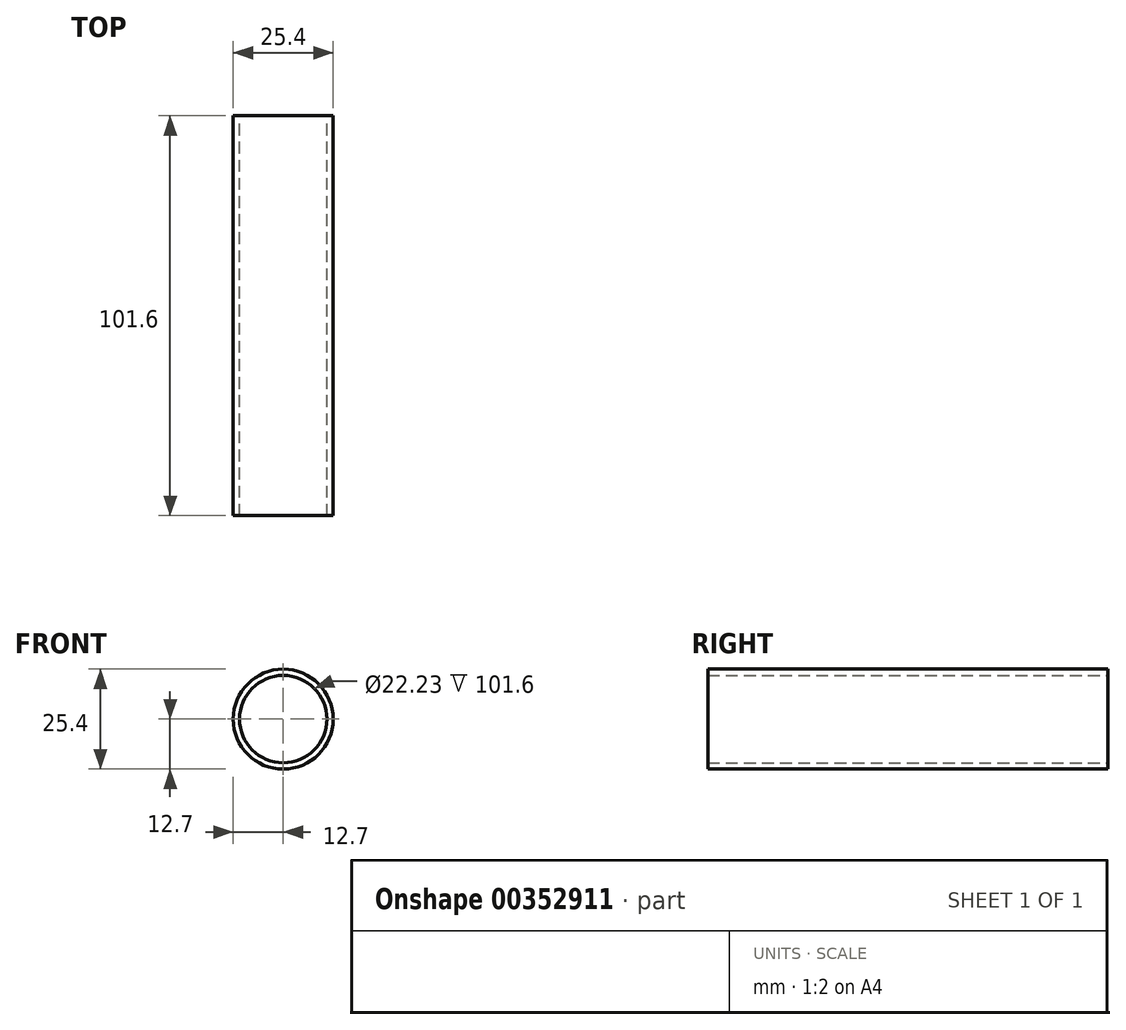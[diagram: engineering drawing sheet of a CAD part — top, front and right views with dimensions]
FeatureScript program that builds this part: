
annotation { "Feature Type Name" : "Feature", "Feature Type Description" : "" }
export const myFeature = defineFeature(function(context is Context, id is Id, definition is map)
    precondition{}
    {
        {
            var Q0;
            Q0=qCreatedBy(makeId("Front.planeOp"),FACE);
            var sketch = newSketch(context, id + "F0", { "sketchPlane" : qUnion([Q0])});
            skCircle(sketch, "E0", {"center": v(0, 0) * mm, "radius": 12.7 * mm});
            skCircle(sketch, "E1", {"center": v(0, 0) * mm, "radius": 11.11 * mm});
            skSolve(sketch);
        }
        {
            var Q0;
            Q0=qSketchRegion(id+"F0",true);
            extrude(context, id + "F1", {"entities" : qUnion([Q0]), "depth" : 101.6 * mm});
        }
    });
